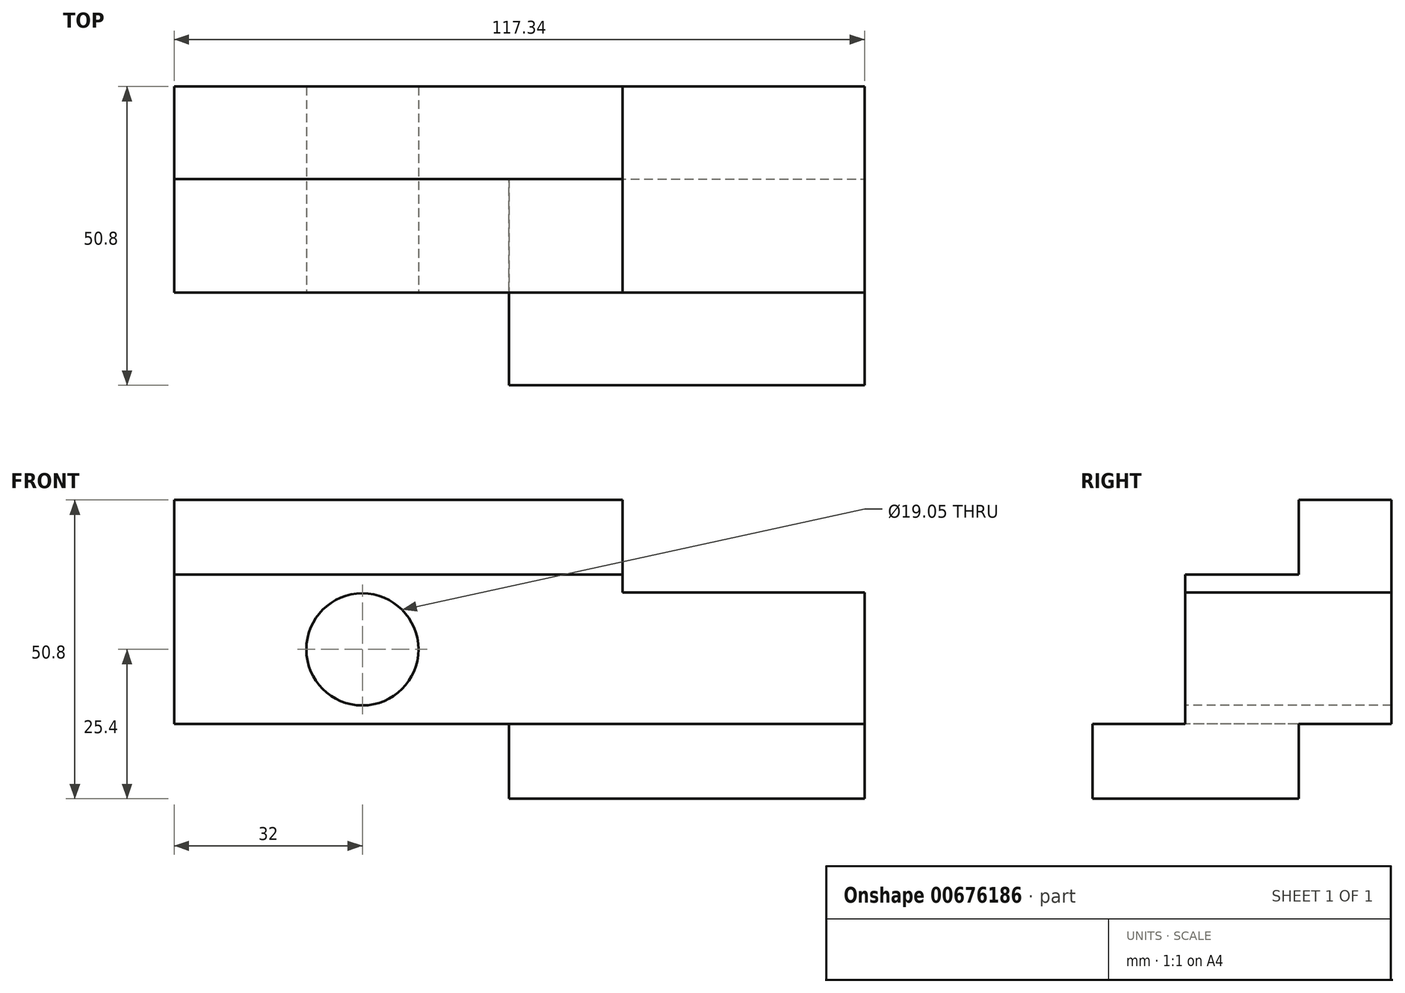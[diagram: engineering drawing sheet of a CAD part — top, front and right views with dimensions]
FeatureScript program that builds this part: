
annotation { "Feature Type Name" : "Feature", "Feature Type Description" : "" }
export const myFeature = defineFeature(function(context is Context, id is Id, definition is map)
    precondition{}
    {
        {
            var Q0;
            Q0=qCreatedBy(makeId("Front.planeOp"),FACE);
            var sketch = newSketch(context, id + "F0", { "sketchPlane" : qUnion([Q0])});
            skLineSegment(sketch, "E0.bottom", {"start": v(-58.67, 25.4) * mm, "end": v(58.67, 25.4) * mm});
            skLineSegment(sketch, "E0.top", {"start": v(-58.67, -25.4) * mm, "end": v(58.67, -25.4) * mm});
            skLineSegment(sketch, "E0.left", {"start": v(-58.67, 25.4) * mm, "end": v(-58.67, -25.4) * mm});
            skLineSegment(sketch, "E0.right", {"start": v(58.67, 25.4) * mm, "end": v(58.67, -25.4) * mm});
            skPoint(sketch, "E0.middle", {"position": v(0, 0) * mm});
            skSolve(sketch);
        }
        {
            var Q0;
            Q0 = qSketchRegion(id + "F0", true);
            extrude(context, id + "F1", {"entities" : qUnion([Q0]), "depth" : 35.05 * mm, "offsetDistance" : 25.4 * mm});
        }
        {
            var Q0;
            Q0=makeQuery(id+"F1.opExtrude","CAP_FACE",FACE,{"disambiguationData":[OSD([sQuery(id+"F0.wireOp",EDGE,"E0.bottom"),sQuery(id+"F0.wireOp",EDGE,"E0.top"),sQuery(id+"F0.wireOp",EDGE,"E0.left"),sQuery(id+"F0.wireOp",EDGE,"E0.right")])],"isStart":false});
            var sketch = newSketch(context, id + "F2", { "sketchPlane" : qUnion([Q0])});
            skLineSegment(sketch, "E1.bottom", {"start": v(-1.78, -25.4) * mm, "end": v(58.67, -25.4) * mm});
            skLineSegment(sketch, "E1.top", {"start": v(-1.78, -12.7) * mm, "end": v(58.67, -12.7) * mm});
            skLineSegment(sketch, "E1.left", {"start": v(-1.78, -25.4) * mm, "end": v(-1.78, -12.7) * mm});
            skLineSegment(sketch, "E1.right", {"start": v(58.67, -25.4) * mm, "end": v(58.67, -12.7) * mm});
            skLineSegment(sketch, "E2.bottom", {"start": v(-58.67, 25.4) * mm, "end": v(17.53, 25.4) * mm});
            skLineSegment(sketch, "E2.top", {"start": v(-58.67, 12.7) * mm, "end": v(17.53, 12.7) * mm});
            skLineSegment(sketch, "E2.left", {"start": v(-58.67, 25.4) * mm, "end": v(-58.67, 12.7) * mm});
            skLineSegment(sketch, "E2.right", {"start": v(17.53, 25.4) * mm, "end": v(17.53, 12.7) * mm});
            skLineSegment(sketch, "E3.bottom", {"start": v(17.53, 25.4) * mm, "end": v(58.67, 25.4) * mm});
            skLineSegment(sketch, "E3.top", {"start": v(17.53, 9.65) * mm, "end": v(58.67, 9.65) * mm});
            skLineSegment(sketch, "E3.left", {"start": v(17.53, 25.4) * mm, "end": v(17.53, 9.65) * mm});
            skLineSegment(sketch, "E3.right", {"start": v(58.67, 25.4) * mm, "end": v(58.67, 9.65) * mm});
            skSolve(sketch);
        }
        {
            var Q0;
            {var subQ3=sQuery(id+"F2.wireOp",EDGE,"E3.bottom");Q0=makeQuery(id+"F2.imprint","IMPRINT",FACE,{"disambiguationData":[TD([[makeQuery(id+"F2.imprint","IMPRINT",EDGE,{"derivedFrom":subQ3}),-1.0]])]});}
            extrude(context, id + "F3", {"entities" : qUnion([Q0]), "operationType" : NewBodyOperationType.REMOVE, "endBound" : BoundingType.THROUGH_ALL, "oppositeDirection" : true, "depth" : 25.4 * mm, "offsetDistance" : 25.4 * mm});
        }
        {
            var Q0;
            {var subQ0=sQuery(id+"F2.wireOp",EDGE,"E2.bottom");Q0=makeQuery(id+"F2.imprint","IMPRINT",FACE,{"disambiguationData":[TD([[makeQuery(id+"F2.imprint","IMPRINT",EDGE,{"derivedFrom":subQ0}),-1.0]])]});}
            extrude(context, id + "F4", {"entities" : qUnion([Q0]), "operationType" : NewBodyOperationType.REMOVE, "oppositeDirection" : true, "depth" : 19.3 * mm, "offsetDistance" : 25.4 * mm});
        }
        {
            var Q0;
            Q0=makeQuery(id+"F2.imprint","IMPRINT",FACE,{"disambiguationData":[TD([[makeQuery(id+"F2.imprint","IMPRINT",EDGE,{"derivedFrom":sQuery(id+"F2.wireOp",EDGE,"E1.bottom")}),1.0]])]});
            extrude(context, id + "F5", {"entities" : qUnion([Q0]), "operationType" : NewBodyOperationType.ADD, "depth" : 15.75 * mm, "offsetDistance" : 25.4 * mm});
        }
        {
            var Q0;
            Q0=makeQuery(id+"F5.boolean.opBoolean","MERGE",FACE,{"derivedFrom":[makeQuery(id+"F1.opExtrude","SWEPT_FACE",FACE,{"disambiguationData":[OSD([sQuery(id+"F0.wireOp",EDGE,"E0.right")])]}),makeQuery(id+"F5.opExtrude","SWEPT_FACE",FACE,{"disambiguationData":[OSD([sQuery(id+"F2.wireOp",EDGE,"E1.right")])]})]});
            var sketch = newSketch(context, id + "F6", { "sketchPlane" : qUnion([Q0])});
            skLineSegment(sketch, "E4.bottom", {"start": v(0, -25.4) * mm, "end": v(-15.75, -25.4) * mm});
            skLineSegment(sketch, "E4.top", {"start": v(0, -12.7) * mm, "end": v(-15.75, -12.7) * mm});
            skLineSegment(sketch, "E4.left", {"start": v(0, -25.4) * mm, "end": v(0, -12.7) * mm});
            skLineSegment(sketch, "E4.right", {"start": v(-15.75, -25.4) * mm, "end": v(-15.75, -12.7) * mm});
            skSolve(sketch);
        }
        {
            var Q0;
            Q0=makeQuery(id+"F6.imprint","IMPRINT",FACE,{"disambiguationData":[TD([[makeQuery(id+"F6.imprint","IMPRINT",EDGE,{"derivedFrom":sQuery(id+"F6.wireOp",EDGE,"E4.bottom")}),1.0]])]});
            extrude(context, id + "F7", {"entities" : qUnion([Q0]), "operationType" : NewBodyOperationType.REMOVE, "endBound" : BoundingType.THROUGH_ALL, "oppositeDirection" : true, "depth" : 25.4 * mm, "offsetDistance" : 25.4 * mm});
        }
        {
            var Q0;
            Q0=makeQuery(id+"F1.opExtrude","CAP_FACE",FACE,{"disambiguationData":[OSD([sQuery(id+"F0.wireOp",EDGE,"E0.bottom"),sQuery(id+"F0.wireOp",EDGE,"E0.top"),sQuery(id+"F0.wireOp",EDGE,"E0.left"),sQuery(id+"F0.wireOp",EDGE,"E0.right")])],"isStart":false});
            var sketch = newSketch(context, id + "F8", { "sketchPlane" : qUnion([Q0])});
            skLineSegment(sketch, "E5.bottom", {"start": v(-1.78, -12.7) * mm, "end": v(-58.67, -12.7) * mm});
            skLineSegment(sketch, "E5.top", {"start": v(-1.78, -25.4) * mm, "end": v(-58.67, -25.4) * mm});
            skLineSegment(sketch, "E5.left", {"start": v(-1.78, -12.7) * mm, "end": v(-1.78, -25.4) * mm});
            skLineSegment(sketch, "E5.right", {"start": v(-58.67, -12.7) * mm, "end": v(-58.67, -25.4) * mm});
            skSolve(sketch);
        }
        {
            var Q0;
            Q0=makeQuery(id+"F8.imprint","IMPRINT",FACE,{"disambiguationData":[TD([[makeQuery(id+"F8.imprint","IMPRINT",EDGE,{"derivedFrom":sQuery(id+"F8.wireOp",EDGE,"E5.bottom")}),1.0]])]});
            extrude(context, id + "F9", {"entities" : qUnion([Q0]), "operationType" : NewBodyOperationType.REMOVE, "endBound" : BoundingType.THROUGH_ALL, "oppositeDirection" : true, "depth" : 25.4 * mm, "offsetDistance" : 25.4 * mm});
        }
        {
            var Q0;
            Q0=makeQuery(id+"F1.opExtrude","CAP_FACE",FACE,{"disambiguationData":[OSD([sQuery(id+"F0.wireOp",EDGE,"E0.bottom"),sQuery(id+"F0.wireOp",EDGE,"E0.top"),sQuery(id+"F0.wireOp",EDGE,"E0.left"),sQuery(id+"F0.wireOp",EDGE,"E0.right")])],"isStart":false});
            var sketch = newSketch(context, id + "F10", { "sketchPlane" : qUnion([Q0])});
            skCircle(sketch, "E6", {"center": v(-26.67, 0) * mm, "radius": 9.53 * mm});
            skSolve(sketch);
        }
        {
            var Q0;
            Q0=makeQuery(id+"F10.imprint","IMPRINT",FACE,{"disambiguationData":[TD([[makeQuery(id+"F10.imprint","IMPRINT",EDGE,{"derivedFrom":sQuery(id+"F10.wireOp",EDGE,"E6")}),1.0]])]});
            extrude(context, id + "F11", {"entities" : qUnion([Q0]), "operationType" : NewBodyOperationType.REMOVE, "endBound" : BoundingType.THROUGH_ALL, "oppositeDirection" : true, "depth" : 25.4 * mm, "offsetDistance" : 25.4 * mm});
        }
    });
